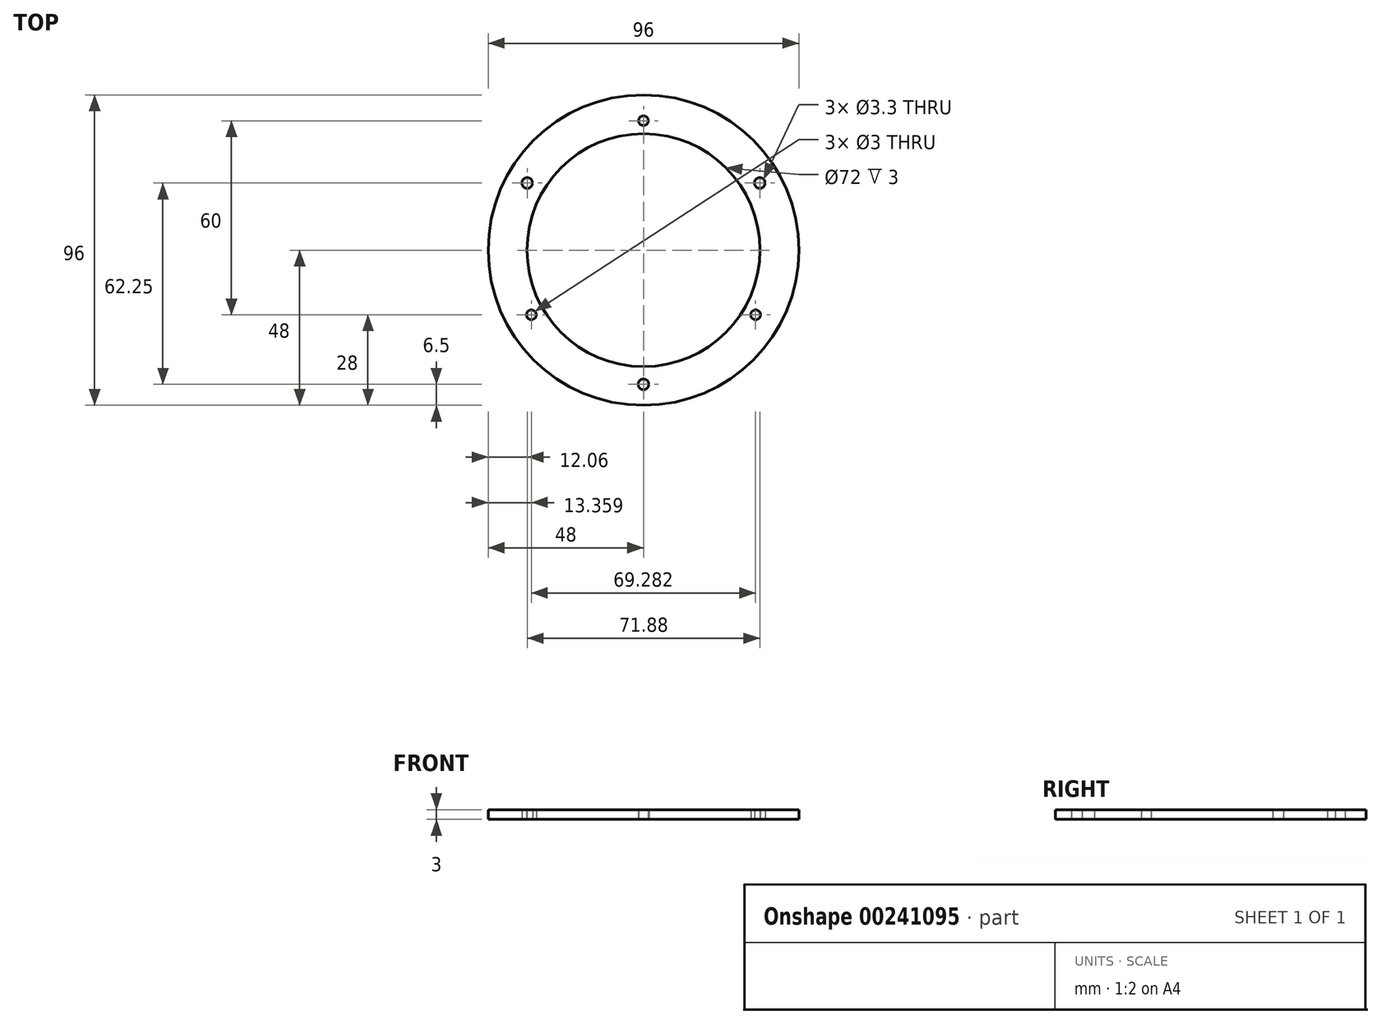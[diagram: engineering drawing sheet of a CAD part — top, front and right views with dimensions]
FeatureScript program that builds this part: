
annotation { "Feature Type Name" : "Feature", "Feature Type Description" : "" }
export const myFeature = defineFeature(function(context is Context, id is Id, definition is map)
    precondition{}
    {
        {
            var Q0;
            Q0=qCreatedBy(makeId("Top.planeOp"),FACE);
            var sketch = newSketch(context, id + "F0", { "sketchPlane" : qUnion([Q0])});
            skCircle(sketch, "E0", {"center": v(0, 0) * mm, "radius": 48 * mm});
            skCircle(sketch, "E1", {"center": v(0, 0) * mm, "radius": 36 * mm});
            skCircle(sketch, "E2", {"center": v(0, -41.5) * mm, "radius": 1.65 * mm});
            skCircle(sketch, "E3.1.0", {"center": v(35.94, 20.75) * mm, "radius": 1.65 * mm});
            skCircle(sketch, "E3.2.0", {"center": v(-35.94, 20.75) * mm, "radius": 1.65 * mm});
            skCircle(sketch, "E4", {"center": v(0, 40) * mm, "radius": 1.5 * mm});
            skCircle(sketch, "E5.1.0", {"center": v(-34.64, -20) * mm, "radius": 1.5 * mm});
            skCircle(sketch, "E5.2.0", {"center": v(34.64, -20) * mm, "radius": 1.5 * mm});
            skSolve(sketch);
        }
        {
            var Q0;
            Q0 = qSketchRegion(id + "F0", true);
            extrude(context, id + "F1", {"entities" : qUnion([Q0]), "depth" : 3 * mm});
        }
    });
